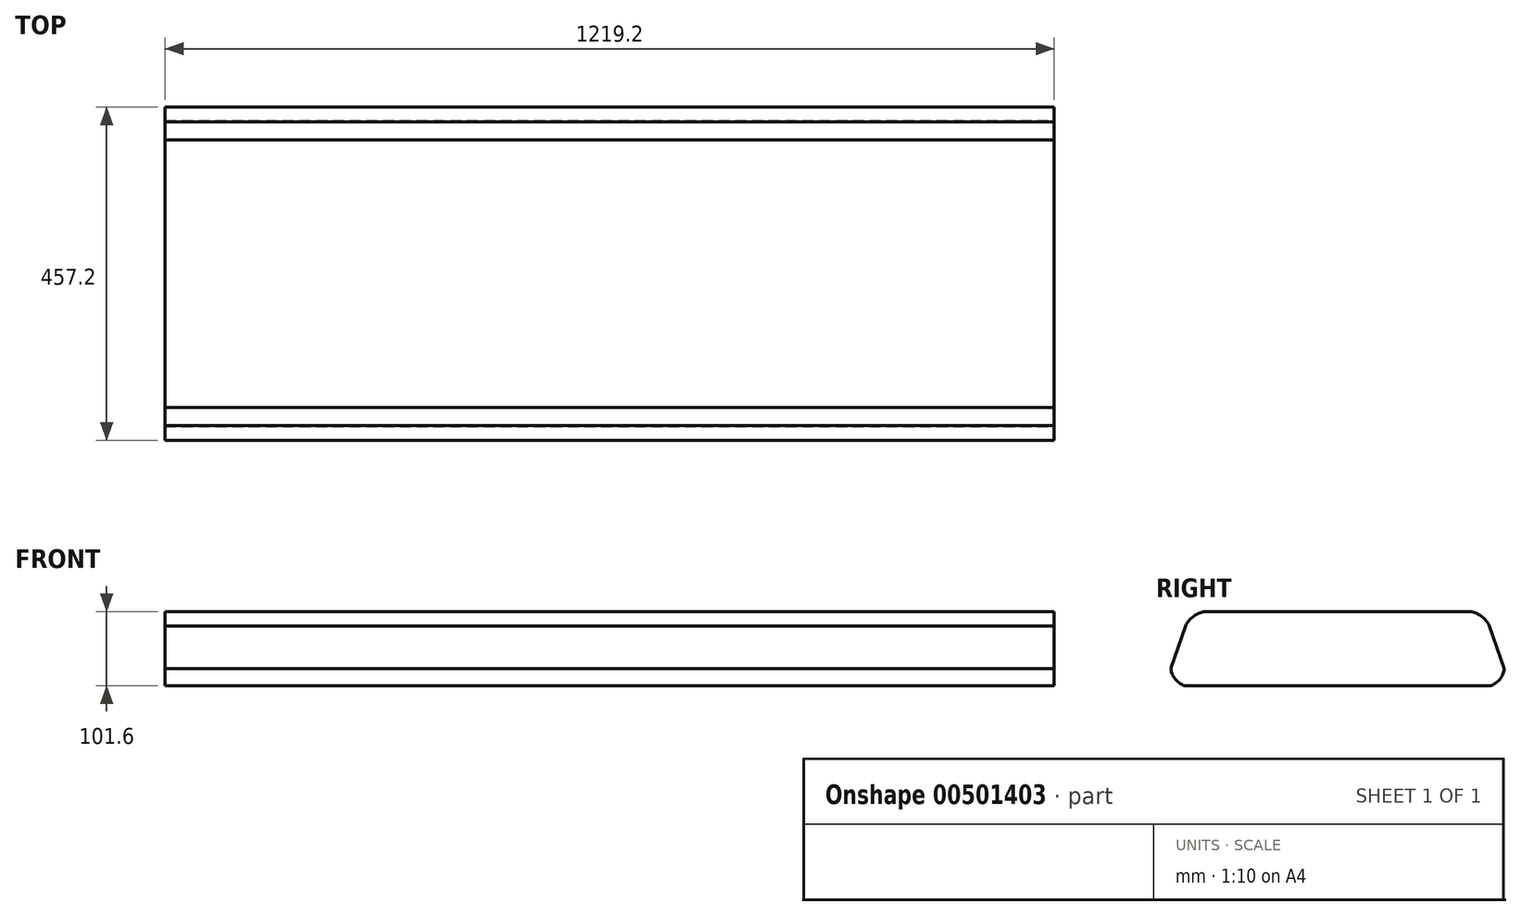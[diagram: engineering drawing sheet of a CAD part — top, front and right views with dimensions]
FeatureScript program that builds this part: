
annotation { "Feature Type Name" : "Feature", "Feature Type Description" : "" }
export const myFeature = defineFeature(function(context is Context, id is Id, definition is map)
    precondition{}
    {
        {
            var Q0;
            Q0=qCreatedBy(makeId("Top.planeOp"),FACE);
            var sketch = newSketch(context, id + "F0", { "sketchPlane" : qUnion([Q0])});
            skLineSegment(sketch, "E0.bottom", {"start": v(0, 0) * mm, "end": v(1219.2, 0) * mm});
            skLineSegment(sketch, "E0.top", {"start": v(0, 457.2) * mm, "end": v(1219.2, 457.2) * mm});
            skLineSegment(sketch, "E0.left", {"start": v(0, 0) * mm, "end": v(0, 457.2) * mm});
            skLineSegment(sketch, "E0.right", {"start": v(1219.2, 0) * mm, "end": v(1219.2, 457.2) * mm});
            skSolve(sketch);
        }
        {
            var Q0;
            Q0 = qSketchRegion(id + "F0", true);
            extrude(context, id + "F1", {"entities" : qUnion([Q0]), "depth" : 101.6 * mm});
        }
        {
            var Q0;
            Q0=makeQuery(id+"F1.opExtrude","SWEPT_FACE",FACE,{"disambiguationData":[OSD([sQuery(id+"F0.wireOp",EDGE,"E0.right")])]});
            var sketch = newSketch(context, id + "F2", { "sketchPlane" : qUnion([Q0])});
            skLineSegment(sketch, "E1", {"start": v(0, 23.27) * mm, "end": v(20.16, 82.07) * mm});
            skLineSegment(sketch, "E2", {"start": v(228.6, 101.6) * mm, "end": v(228.6, 0) * mm, "construction": true});
            skArc(sketch, "E3", {"start": v(44.93, 101.6) * mm, "mid": v(30.37, 94.6) * mm, "end": v(20.16, 82.07) * mm});
            skArc(sketch, "E4", {"start": v(0, 23.27) * mm, "mid": v(5.98, 8.9) * mm, "end": v(18.73, 0) * mm});
            skLineSegment(sketch, "E5", {"start": v(18.73, 0) * mm, "end": v(0, 0) * mm});
            skLineSegment(sketch, "E6", {"start": v(0, 0) * mm, "end": v(0, 101.6) * mm});
            skLineSegment(sketch, "E7", {"start": v(0, 101.6) * mm, "end": v(26.85, 101.6) * mm});
            skArc(sketch, "E8.MirrorCS", {"start": v(412.27, 101.6) * mm, "mid": v(426.83, 94.6) * mm, "end": v(437.04, 82.07) * mm});
            skLineSegment(sketch, "E9.MirrorCS", {"start": v(457.2, 23.27) * mm, "end": v(430.35, 101.6) * mm});
            skArc(sketch, "E10.MirrorCS", {"start": v(457.2, 23.27) * mm, "mid": v(451.22, 8.9) * mm, "end": v(438.47, 0) * mm});
            skLineSegment(sketch, "E11", {"start": v(412.27, 101.6) * mm, "end": v(457.2, 101.6) * mm});
            skLineSegment(sketch, "E12", {"start": v(457.2, 101.6) * mm, "end": v(457.2, 0) * mm});
            skLineSegment(sketch, "E13", {"start": v(457.2, 0) * mm, "end": v(438.47, 0) * mm});
            skLineSegment(sketch, "E14", {"start": v(26.85, 101.6) * mm, "end": v(44.93, 101.6) * mm});
            skSolve(sketch);
        }
        {
            var Q0;
            Q0 = qSketchRegion(id + "F2", true);
            extrude(context, id + "F3", {"entities" : qUnion([Q0]), "operationType" : NewBodyOperationType.REMOVE, "endBound" : BoundingType.UP_TO_NEXT, "oppositeDirection" : true, "depth" : 25.4 * mm});
        }
    });
